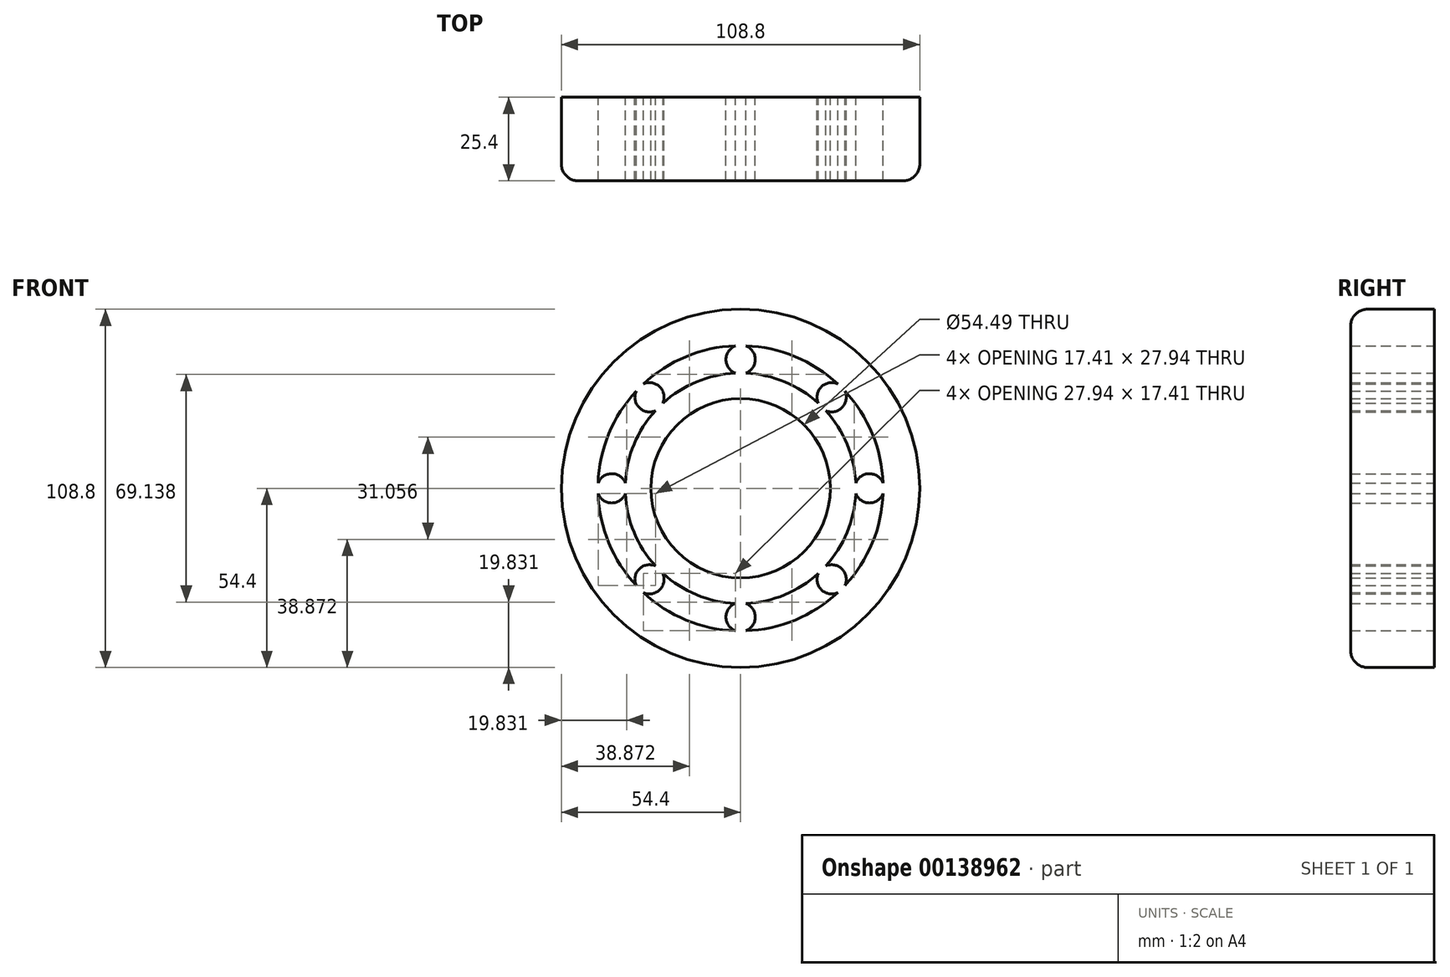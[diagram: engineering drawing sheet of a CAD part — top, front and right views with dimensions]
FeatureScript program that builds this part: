
annotation { "Feature Type Name" : "Feature", "Feature Type Description" : "" }
export const myFeature = defineFeature(function(context is Context, id is Id, definition is map)
    precondition{}
    {
        {
            var Q0;
            Q0=qCreatedBy(makeId("Front.planeOp"),FACE);
            var sketch = newSketch(context, id + "F0", { "sketchPlane" : qUnion([Q0])});
            skCircle(sketch, "E0", {"center": v(0, 0) * mm, "radius": 54.4 * mm});
            skCircle(sketch, "E1", {"center": v(0, 0) * mm, "radius": 43.3 * mm});
            skSolve(sketch);
        }
        {
            var Q0;
            Q0 = qSketchRegion(id + "F0", true);
            extrude(context, id + "F1", {"entities" : qUnion([Q0]), "depth" : 25.4 * mm});
        }
        {
            var Q0;
            Q0=qCreatedBy(makeId("Front.planeOp"),FACE);
            var sketch = newSketch(context, id + "F2", { "sketchPlane" : qUnion([Q0])});
            skCircle(sketch, "E2", {"center": v(0, 0) * mm, "radius": 35 * mm});
            skCircle(sketch, "E3", {"center": v(0, 0) * mm, "radius": 27.24 * mm});
            skSolve(sketch);
        }
        {
            var Q0;
            Q0 = qSketchRegion(id + "F2", true);
            extrude(context, id + "F3", {"entities" : qUnion([Q0]), "depth" : 25.4 * mm});
        }
        {
            var Q0;
            Q0=qCreatedBy(makeId("Front.planeOp"),FACE);
            var sketch = newSketch(context, id + "F4", { "sketchPlane" : qUnion([Q0])});
            skCircle(sketch, "E4", {"center": v(0, 39.11) * mm, "radius": 4.45 * mm});
            skCircle(sketch, "E5.1.0", {"center": v(-27.66, 27.66) * mm, "radius": 4.45 * mm});
            skCircle(sketch, "E5.2.0", {"center": v(-39.11, 0) * mm, "radius": 4.45 * mm});
            skCircle(sketch, "E5.3.0", {"center": v(-27.66, -27.66) * mm, "radius": 4.45 * mm});
            skCircle(sketch, "E5.4.0", {"center": v(0, -39.11) * mm, "radius": 4.45 * mm});
            skCircle(sketch, "E5.5.0", {"center": v(27.66, -27.66) * mm, "radius": 4.45 * mm});
            skCircle(sketch, "E5.6.0", {"center": v(39.11, 0) * mm, "radius": 4.45 * mm});
            skCircle(sketch, "E5.7.0", {"center": v(27.66, 27.66) * mm, "radius": 4.45 * mm});
            skPoint(sketch, "E5.center", {"position": v(0, 0) * mm});
            skSolve(sketch);
        }
        {
            var Q0;
            Q0 = qSketchRegion(id + "F4", true);
            extrude(context, id + "F5", {"entities" : qUnion([Q0]), "operationType" : NewBodyOperationType.ADD, "depth" : 25.4 * mm});
        }
        {
            var Q0;
            Q0=makeQuery(id+"F1.opExtrude","CAP_EDGE",EDGE,{"disambiguationData":[OSD([sQuery(id+"F0.wireOp",EDGE,"E0")])],"isStart":false});
            fillet(context, id + "F6", {"entities" : qUnion([Q0]), "radius" : 5.08 * mm, "tangentPropagation" : true, "allowEdgeOverflow" : false});
        }
    });
